# Revit family: Flush_Valve-AC_Urinal-American_Standard-Exposed-Top_Spud-606B_Series
name_source: partatom
category: Plumbing Fixtures
revit_build: Autodesk Revit 2014 (Build: 20130308_1515(x64)
units: mm (PartAtom-declared; Revit-internal decimal feet)

## types (4) — shared parameters
ADA Compliant = Yes
Assembly Code = D2020100
CW Connection = Yes
CWFU = 5
Cold Water Connection Diameter = 3/4"
Cold Water Connection Height = 11 1/2"
Cold Water Connection Radius = 3/8"
Cold Water Connection Width = 4 3/4"
Default Elevation = 0"
Description = Selectronic Sensor Operated Urinal Flush Valve
Electrical Box & Cover Height = 23 3/8"
Electrical Box & Cover Width = 8 1/2"
HW Connection = No
Height = 16 1/8"
Installation Type = Exposed
Length = 2 1/4"
Manufacturer = American Standard
Material = Metal-American Standard-002-Polished Chrome
PK00.BBU - Battery Back-Up = Yes
PK00.HAC - Hard Wired AC - Power Kit = No
PK00.MAC - Multi-AC - Power Kit = No
Price = Prices may vary. Please consult Manufacturer Representative for most up-to-date price list.
Product Documentation Link = https://www.americanstandard-us.com
Product Page URL = https://www.americanstandard-us.com
Revised Date = 12/23/2016
URL = http://www.americanstandard-us.com
Vent Connection = No
Warranty Information = 1 Year Limited Warranty
Waste Connection = No
Width = 2 7/8"
zero-valued in all types: HWFU, WFU

## per-type parameters (varying)
| type | Flush Rate |
| 606B.101 | 1.0 gpf/3.8 Lpf |
| 606B.051 | 0.5 gpf/1.9 Lpf |
| 606B.025 | 0.25 gpf/1.0 Lpf |
| 606B.013 | 0.125 gpf/0.5 Lpf |

note: column(s) folded — value = type name in every type: Model

## geometry (parser evidence)
native form markers: Sweep x2
no freeform markers — native parametric forms only
